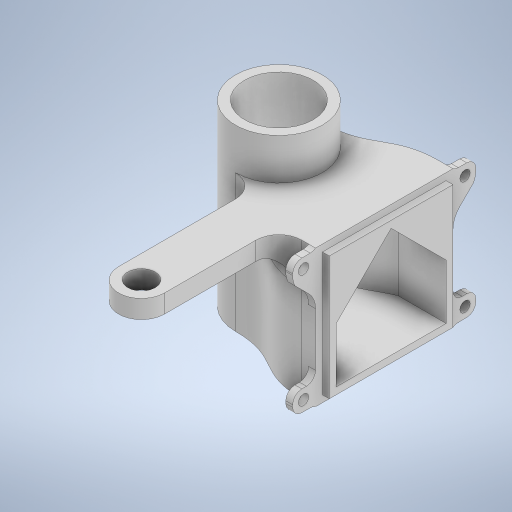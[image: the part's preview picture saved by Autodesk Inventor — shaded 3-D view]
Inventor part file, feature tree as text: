
AUTODESK INVENTOR PART (.ipt)
format: ipt  version: 2024 (Build 280153000, 153)  size: 533,504 bytes
history: native  units: in
note: dims shown in document units (in); Inventor stores cm internally (conversion verified against a paired STEP export)
features: extrude x8, sketch x7, fillet x4, projected_geometry x3, plane x1, hole x1, chamfer x1
ambient origin geometry x8: Origin, YZ Plane, XZ Plane, XY Plane, X Axis, Y Axis, Z Axis, Center Point
bodies: Solid1 (feature_tree)
feature tree (25):
  extrude  "Extrusion1"  Depth=0.0787in
  plane  "Work Plane1"
  extrude  "Extrusion2"  Depth=0.374in
  sketch  "Sketch4"  dims[d5=1.1811in d6=0.1181in]
  extrude  "Extrusion4"  Depth=0.1181in
  hole  "Hole2"  [1 undecoded]
  sketch  "Sketch9"  dims[d10=0.4724in d11=0.1181in]
  extrude  "Extrusion7"  Depth=0.1181in
  extrude  "Extrusion8"  Depth=1.1811in
  extrude  "Extrusion9"  Depth=0.5906in TaperAngle=0.0deg
  extrude  "Extrusion3"  Depth=0.0886in
  fillet  "Fillet1"  Radius=1.1811in
  chamfer  "Chamfer1"  Distance=1.1811in
  fillet  "Fillet2"  Radius=0.0591in
  extrude  "Extrusion10"  Depth=0.2362in TaperAngle=0.0deg
  fillet  "Fillet3"  Radius=0.0591in
  fillet  "Fillet4"  Radius=0.748in
  sketch  "Sketch1"  dims[d0=0.748in d1=0.0787in]
  sketch  "Sketch2"  dims[d2=0.4724in d3=0.0in d4=0.374in]
  projected_geometry  "Projected Loop1"
  sketch  "Sketch8"  dims[d7=0.1181in d9=0.9449in]
  projected_geometry  "Projected Loop5"
  sketch  "Sketch11"  dims[d12=0.1181in d13=1.1811in]
  sketch  "Sketch12"  dims[d20=0.1181in d23=0.5906in d24=0.0in d25=0.0886in d26=1.1811in d27=1.1811in d35=0.0591in d36=0.2362in d37=0.0in d38=0.0591in d39=0.0in d40=0.748in d41=0.0in d53=0.5906in d54=0.1033in d55=0.1033in d56=0.1033in d57=0.1033in d58=0.1033in d60=0.1033in d61=0.1033in d62=0.5906in d63=0.2362in d64=0.1575in d65=0.0787in d66=90.0deg d67=0.3937in d68=0.8108in d69=0.7874in d70=0.0787in d71=0.0787in d72=0.0in d73=0.0in d74=1.1811in d75=0.0in d76=0.1033in d77=0.1033in d78=0.1033in d79=0.1033in d80=0.1772in d82=0.1772in d86=0.0591in d87=0.0in d91=0.0787in d92=0.0148in d93=0.0886in d94=0.1969in d95=0.1969in d99=0.0148in d100=0.1772in d101=0.0787in d102=45.0deg d103=0.1969in d104=0.4724in d105=0.4724in d106=0.4724in d107=0.2362in d108=0.3937in d109=1.5748in d110=0.3937in d111=0.1969in d113=0.1969in d114=0.1575in d115=0.0in d116=0.1969in d117=0.1969in]
  projected_geometry  "Projected Loop6"
note: 1 required parameter value undecoded (feature->parameter linkage not recoverable at this tier; creation-order binding heuristic only, values carry confidence <= 0.55)
